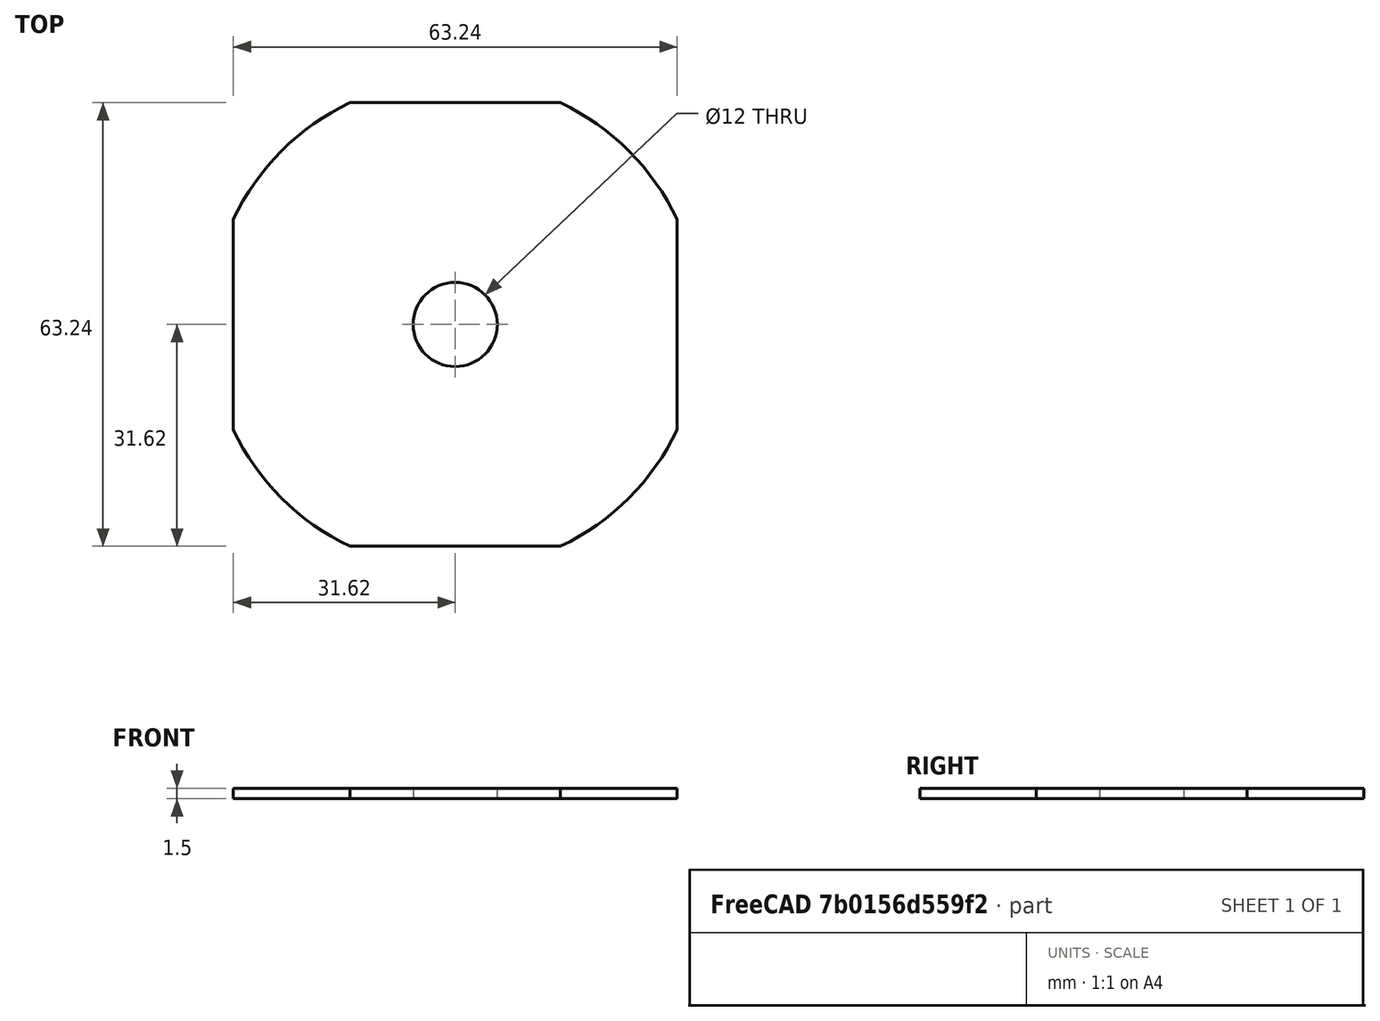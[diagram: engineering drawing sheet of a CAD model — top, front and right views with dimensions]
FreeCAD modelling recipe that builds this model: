
FCSTD DOCUMENT  (FreeCAD 0.14R3700 (Git))
Label: BIRR_PCB_disc
License: CC-BY 3.0
LicenseURL: http://creativecommons.org/licenses/by/3.0/
objects: Sketcher::SketchObject×1, Part::Extrusion×1, Part::Feature×1
note: 3 computed .brp shape members not serialized (recipe doc carries the construction recipe); baked Part::Feature solids carry a one-line shape summary decoded from their .brp

FEATURE [Sketcher::SketchObject] Sketch  label="PCB_disc"
  sketch-geometry (9):
    g0: Circle CenterX=0 CenterY=0 CenterZ=0 NormalX=0 NormalY=0 NormalZ=1 Radius=6
    g1: ArcOfCircle CenterX=0 CenterY=0 CenterZ=0 NormalX=0 NormalY=0 NormalZ=1 Radius=35 StartAngle=0.442911 EndAngle=1.12789
    g2: LineSegment StartX=15 StartY=31.6228 StartZ=0 EndX=-15 EndY=31.6228 EndZ=0
    g3: LineSegment StartX=31.6228 StartY=15 StartZ=0 EndX=31.6228 EndY=-15 EndZ=0
    g4: ArcOfCircle CenterX=0 CenterY=0 CenterZ=0 NormalX=0 NormalY=0 NormalZ=1 Radius=35 StartAngle=5.1553 EndAngle=5.84027
    g5: ArcOfCircle CenterX=0 CenterY=0 CenterZ=0 NormalX=0 NormalY=0 NormalZ=1 Radius=35 StartAngle=2.01371 EndAngle=2.69868
    g6: LineSegment StartX=-31.6228 StartY=15 StartZ=0 EndX=-31.6228 EndY=-15 EndZ=0
    g7: ArcOfCircle CenterX=0 CenterY=0 CenterZ=0 NormalX=0 NormalY=0 NormalZ=1 Radius=35 StartAngle=3.5845 EndAngle=4.26948
    g8: LineSegment StartX=-15 StartY=-31.6228 StartZ=0 EndX=15 EndY=-31.6228 EndZ=0
  constraints (23):
    c: Coincident(g0,g-1)
    c: Radius(g0) = 6
    c: Coincident(g1,g-1)
    c: Radius(g1) = 35
    c: Coincident(g2,g1)
    c: Coincident(g3,g1)
    c: Coincident(g4,g-1)
    c: Coincident(g4,g3)
    c: Coincident(g5,g-1)
    c: Coincident(g5,g2)
    c: Coincident(g6,g5)
    c: Coincident(g7,g-1)
    c: Coincident(g7,g6)
    c: Coincident(g8,g7)
    c: Coincident(g8,g4)
    c: Symmetric(g1,g3,g-1)
    c: Symmetric(g1,g2,g-2)
    c: Symmetric(g5,g6,g-1)
    c: Symmetric(g7,g4,g-2)
    c: DistanceY(g3) = -30
    c: DistanceX(g2) = -30
    c: DistanceY(g6) = -30
    c: DistanceX(g8) = 30
FEATURE [Part::Extrusion] Extrude
  Base = -> Sketch
  Dir = (0,0,1.5)
  Solid = true
FEATURE [Part::Feature] Extrude001  label="PCB_disc_copy"
  shape: bbox 63.25 x 63.25 x 1.5 mm, 11 faces (baked)
